# Revit family: LAMP_B-SIDE 135
name_source: partatom
category: Luminarias
revit_build: Autodesk Revit LT 2015 (Build: 20140606_1530(x64)
units: mm (PartAtom-declared; Revit-internal decimal feet)

## types (2) — shared parameters
CRI = 80
Cambio de temperatura de color de luz atenuada = <Ninguno>
Diameter = 160 mm  [stored 0.524934 ft]
Efficacy = 33 lm/W
Elevación por defecto = 1219 mm
Fabricante = LAMP
Filtro de color = 16777215
Gear = Electronic
Height = 135 mm  [stored 0.442913 ft]
IEE = A++
Installation instructions = https://www.lamp.es
Insulation class = I
LED Lifetime = 50.000 L70 B10
Last update = 21/12/2020
Luminaire type = Outdoor - Beacon
Lámpara = HIGH POWER LED
HIGH POWER LED
HIGH POWER LED
HIGH POWER LED
Manufacturer URL = http://www.lamp.es
Manufacturer country = Spain
Manufacturer name = LAMP
Plum = 4 W
Power = 2 W
Power Supply = 110-240V 50-60Hz
Product URL = https://www.lamp.es
Protection rating = IP65 / IK10
Type = HI POWER CREE
Weight = 1.45 kg
Ángulo de inclinación = 90.00°

## per-type parameters (varying)
| type | Archivo de red fotométrica | Descripción | Finish | Material | Modelo | Product code | Product datasheet |
| 115LM 4000 BLACK | 5841254.IES | B-SIDE LED 135 250 NW ANT. | Textured anthracite grey | LAMP_Aluminio B-Side antracita | BS1DB1303840NA | BS1DB1303840NA | http://www.lamp.https: |
| 115LM 4000 GREY | 5841253.IES | B-SIDE LED 135 250 NW GR. | Texturised grey | LAMP_Aluminio B-Side gris | BS1DB1303840NG | BS1DB1303840NG | http://www.lamp.es |

note: [stored X ft] marks values corroborated as IEEE doubles in the binary element streams (Revit-internal decimal feet)
